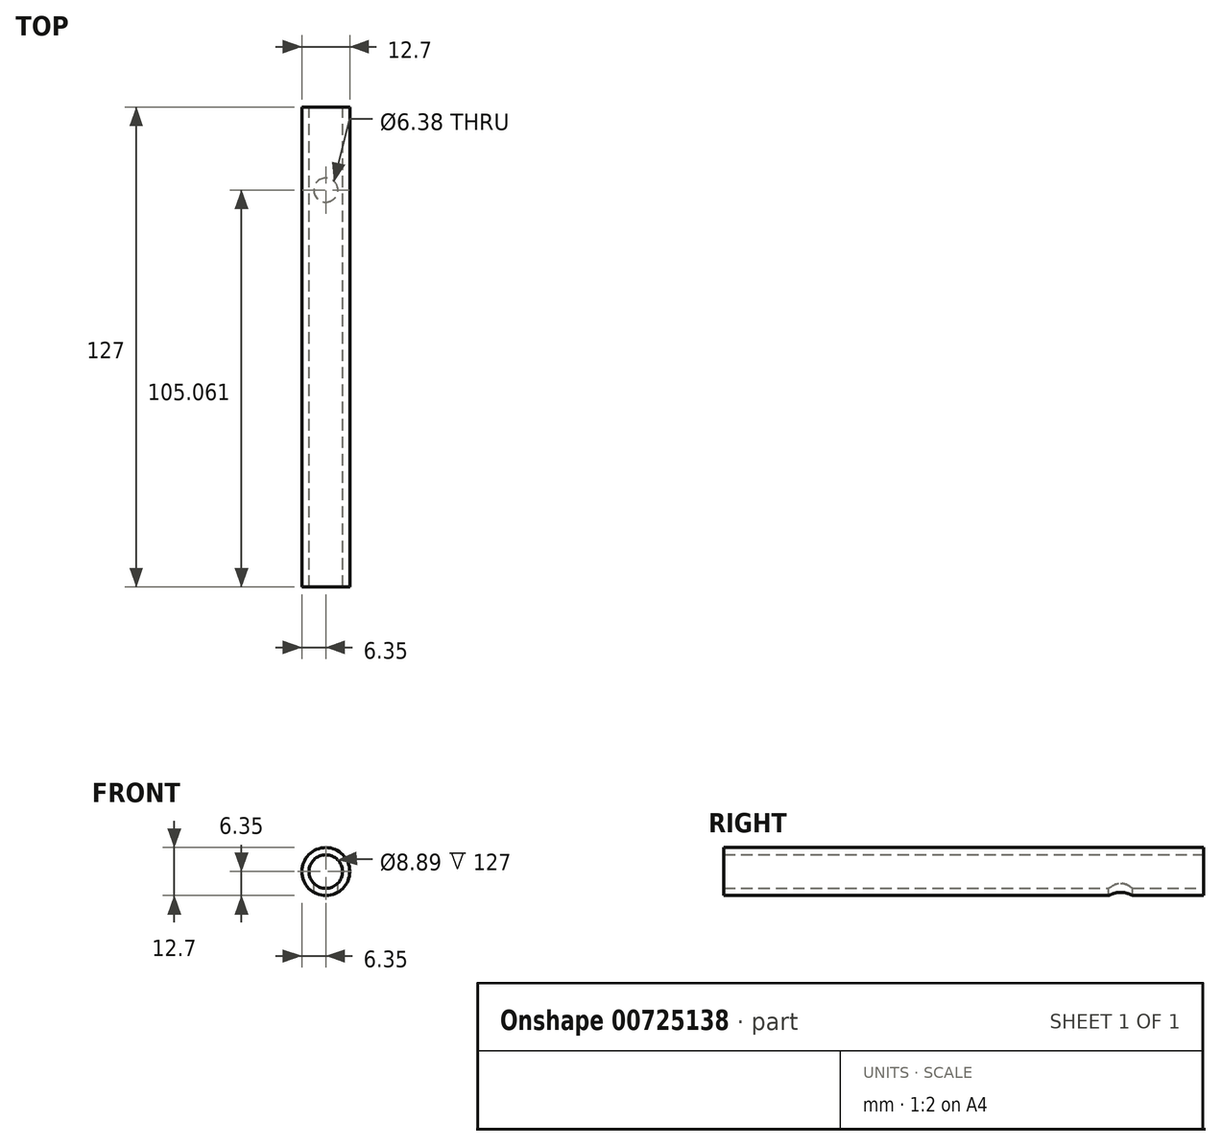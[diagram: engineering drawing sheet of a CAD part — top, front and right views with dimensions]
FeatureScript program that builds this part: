
annotation { "Feature Type Name" : "Feature", "Feature Type Description" : "" }
export const myFeature = defineFeature(function(context is Context, id is Id, definition is map)
    precondition{}
    {
        {
            var Q0;
            Q0=qCreatedBy(makeId("Front.planeOp"),FACE);
            var sketch = newSketch(context, id + "F0", { "sketchPlane" : qUnion([Q0])});
            skCircle(sketch, "E0", {"center": v(0, 0) * mm, "radius": 6.35 * mm});
            skSolve(sketch);
        }
        {
            var Q0;
            Q0=makeQuery(id+"F0.imprint","IMPRINT",FACE,{"disambiguationData":[TD([[makeQuery(id+"F0.imprint","IMPRINT",EDGE,{"derivedFrom":sQuery(id+"F0.wireOp",EDGE,"E0")}),1.0]])]});
            extrude(context, id + "F1", {"entities" : qUnion([Q0]), "depth" : 127 * mm, "offsetDistance" : 25.4 * mm});
        }
        {
            var Q0;
            Q0=qCreatedBy(makeId("Front.planeOp"),FACE);
            var sketch = newSketch(context, id + "F2", { "sketchPlane" : qUnion([Q0])});
            skCircle(sketch, "E1", {"center": v(0, 0) * mm, "radius": 4.45 * mm});
            skSolve(sketch);
        }
        {
            var Q0;
            Q0=makeQuery(id+"F2.imprint","IMPRINT",FACE,{"disambiguationData":[TD([[makeQuery(id+"F2.imprint","IMPRINT",EDGE,{"derivedFrom":sQuery(id+"F2.wireOp",EDGE,"E1")}),1.0]])]});
            extrude(context, id + "F3", {"entities" : qUnion([Q0]), "operationType" : NewBodyOperationType.REMOVE, "depth" : 127 * mm, "offsetDistance" : 25.4 * mm});
        }
        {
            var Q0;
            Q0=qCreatedBy(makeId("Top.planeOp"),FACE);
            var sketch = newSketch(context, id + "F4", { "sketchPlane" : qUnion([Q0])});
            skCircle(sketch, "E2", {"center": v(0, -21.94) * mm, "radius": 3.19 * mm});
            skSolve(sketch);
        }
        {
            var Q0;
            Q0 = qSketchRegion(id + "F4", true);
            extrude(context, id + "F5", {"entities" : qUnion([Q0]), "operationType" : NewBodyOperationType.REMOVE, "endBound" : BoundingType.THROUGH_ALL, "oppositeDirection" : true, "depth" : 25.4 * mm, "offsetDistance" : 25.4 * mm});
        }
    });
